# Revit family: 510201 SMART COMMAND ELECTRONIC SHOWER 1 OUTLET
name_source: partatom
category: Plumbing Fixtures
revit_build: Autodesk Revit 2016 (Build: 20161004_0715(x64)
units: mm (PartAtom-declared; Revit-internal decimal feet)

## family parameters
Cut with Voids When Loaded = No
Host = Face
OmniClass Number = 23.45.55.11
OmniClass Title = Sanitary Components
Part Type = Normal
Room Calculation Point = No
Round Connector Dimension = Use Radius
Shared = No

## types (1)
- SMART COMMAND ELECTRONIC SHOWER 1 OUTLET
    Assembly Code = C1030210
    CW Connection = Yes
    Default Elevation = 900 mm
    Description = SMART COMMAND ELECTRONIC SHOWER 1 OUTLET
    HW Connection = Yes
    Manufacturer = GWA Bathrooms & Kitchens
    Material_Base = GWA-Metal-White
    Material_Connections = GWA_Metal-Chrome
    Material_CoverPlate = GWA-Glass-Black
    Material_Elect_Connection = GWA-Plastic-Black
    Material_Enclosure = GWA-Plastic-Black
    Model = 510201
    URL = https://www.caroma.com.au
    Vent Connection = No
    Waste Connection = No

## geometry (parser evidence)
native form markers: Sweep x1
no freeform markers — native parametric forms only
